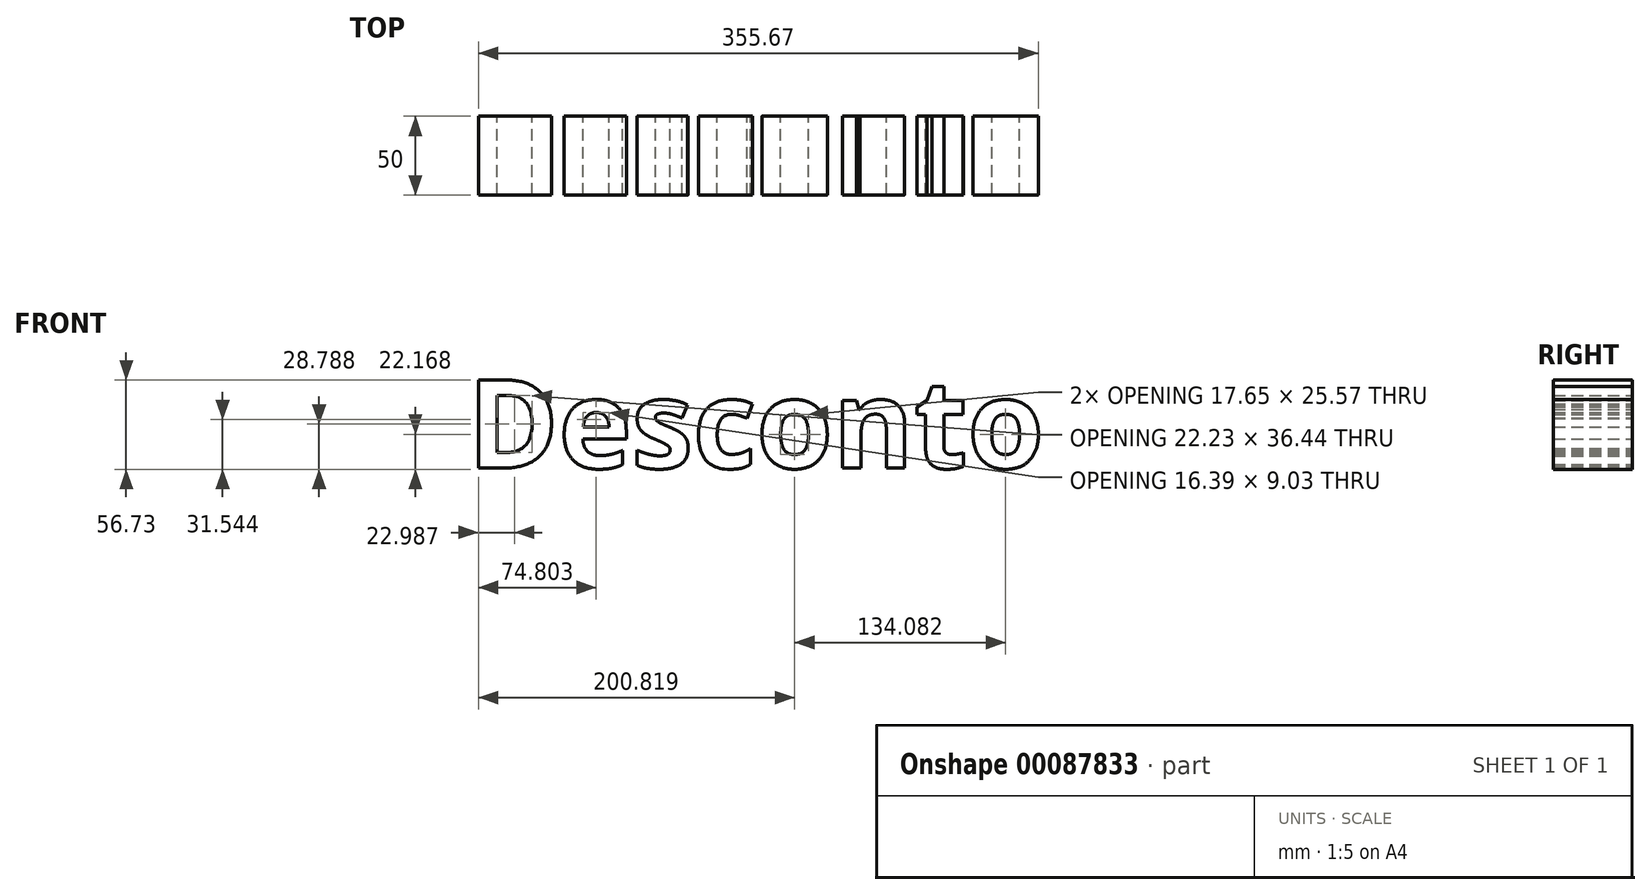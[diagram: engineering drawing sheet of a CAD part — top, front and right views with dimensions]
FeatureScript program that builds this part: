
annotation { "Feature Type Name" : "Feature", "Feature Type Description" : "" }
export const myFeature = defineFeature(function(context is Context, id is Id, definition is map)
    precondition{}
    {
        {
            var Q0;
            Q0=qCreatedBy(makeId("Front.planeOp"),FACE);
            var sketch = newSketch(context, id + "F0", { "sketchPlane" : qUnion([Q0])});
            skText(sketch, "E0", { "text": "Desconto", "fontName": "OpenSans-Bold.ttf"});
            const initialGuessF0  = {"E0": [-0.15788, -0.03366, 1, 0, 0.05644]};
            skSetInitialGuess(sketch, initialGuessF0);
            skSolve(sketch);
        }
        {
            var Q0;
            Q0 = qSketchRegion(id + "F0", true);
            extrude(context, id + "F1", {"entities" : qUnion([Q0]), "endBound" : BoundingType.SYMMETRIC, "depth" : 50 * mm});
        }
    });
